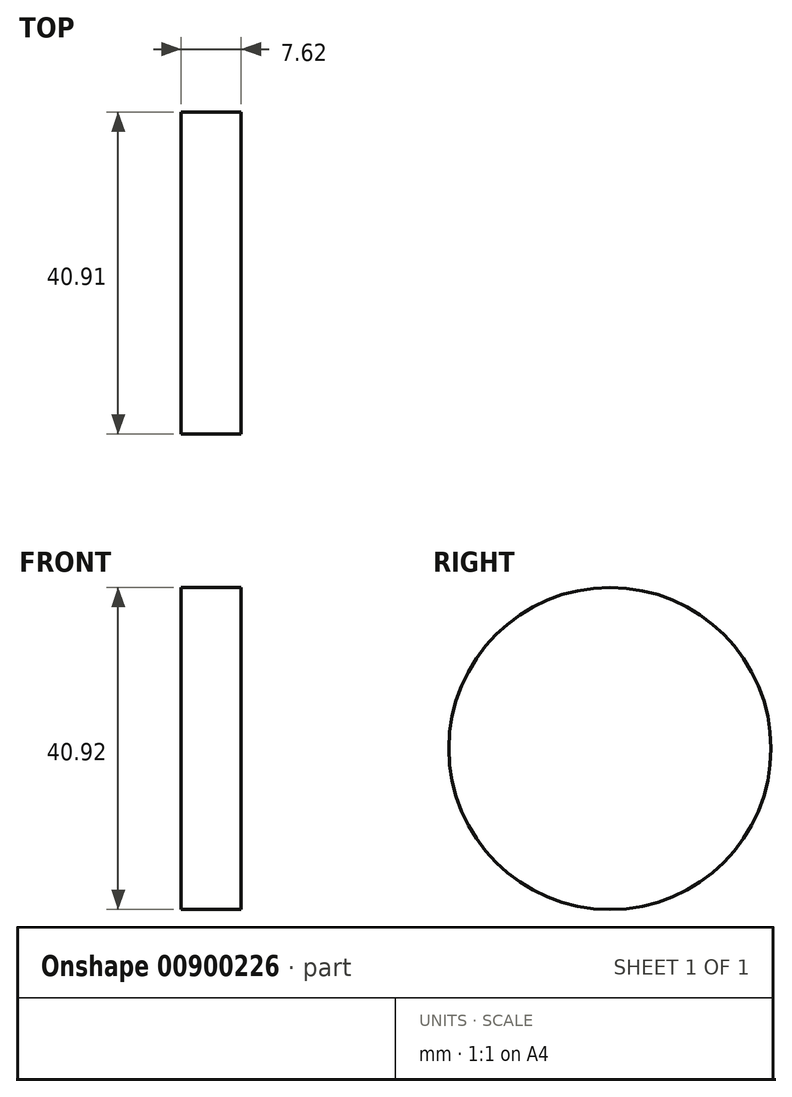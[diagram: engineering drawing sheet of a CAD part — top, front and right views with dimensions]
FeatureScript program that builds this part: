
annotation { "Feature Type Name" : "Feature", "Feature Type Description" : "" }
export const myFeature = defineFeature(function(context is Context, id is Id, definition is map)
    precondition{}
    {
        {
            var Q0;
            Q0=qCreatedBy(makeId("Right.planeOp"),FACE);
            var sketch = newSketch(context, id + "F0", { "sketchPlane" : qUnion([Q0])});
            skCircle(sketch, "E0", {"center": v(-37.9, -14.26) * mm, "radius": 20.46 * mm});
            skSolve(sketch);
        }
        {
            var Q0;
            Q0=makeQuery(id+"F0.imprint","IMPRINT",FACE,{"disambiguationData":[TD([[makeQuery(id+"F0.imprint","IMPRINT",EDGE,{"derivedFrom":sQuery(id+"F0.wireOp",EDGE,"E0")}),1.0]])]});
            extrude(context, id + "F1", {"entities" : qUnion([Q0]), "depth" : 7.62 * mm, "offsetDistance" : 25.4 * mm});
        }
    });
